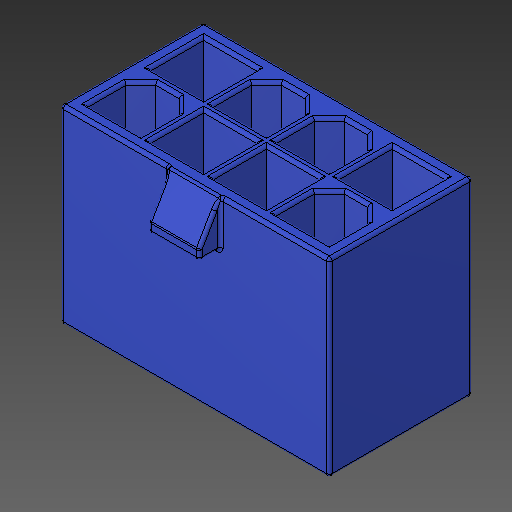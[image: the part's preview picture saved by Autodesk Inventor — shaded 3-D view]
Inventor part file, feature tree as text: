
AUTODESK INVENTOR PART (.ipt)
format: ipt  version: 2018.2 (Build 222227000, 227)  size: 205,824 bytes
history: native  units: mm
features: other x1, fillet x1
ambient origin geometry x8: Origin, YZ Plane, XZ Plane, XY Plane, X Axis, Y Axis, Z Axis, Center Point
bodies: Body1 (feature_tree)
feature tree (2):
  other  "ソリッド1"
  fillet  "Fillet1"  [1 undecoded]
note: 1 required parameter value undecoded (feature->parameter linkage not recoverable at this tier; creation-order binding heuristic only, values carry confidence <= 0.55)
